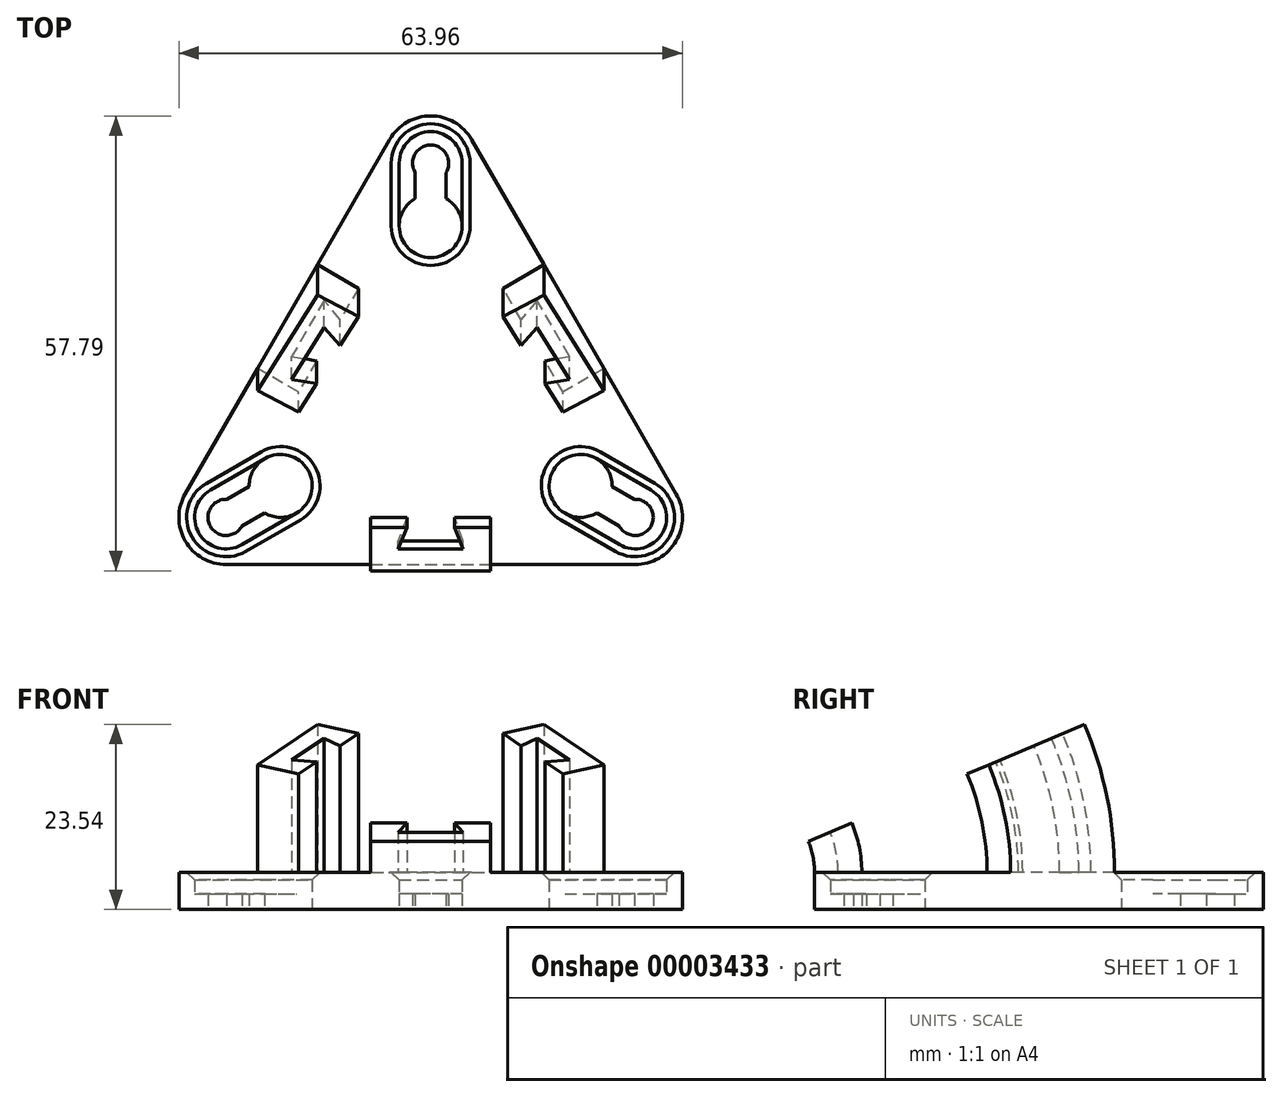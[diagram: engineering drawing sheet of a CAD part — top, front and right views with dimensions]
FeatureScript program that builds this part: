
annotation { "Feature Type Name" : "Feature", "Feature Type Description" : "" }
export const myFeature = defineFeature(function(context is Context, id is Id, definition is map)
    precondition{}
    {
        {
            var Q0;
            Q0=qCreatedBy(makeId("Top.planeOp"),FACE);
            cPlane(context, id + "F0", {"entities" : qUnion([Q0]), "cplaneType" : CPlaneType.OFFSET, "offset" : 2 * mm, "width" : 150 * mm, "height" : 150 * mm});
        }
        {
            var Q0;
            Q0=qCreatedBy(id+"F0.planeOp",FACE);
            cPlane(context, id + "F1", {"entities" : qUnion([Q0]), "cplaneType" : CPlaneType.OFFSET, "offset" : 2.75 * mm, "width" : 150 * mm, "height" : 150 * mm});
        }
        {
            var Q0;
            Q0=qCreatedBy(makeId("Top.planeOp"),FACE);
            var sketch = newSketch(context, id + "F2", { "sketchPlane" : qUnion([Q0])});
            skCircle(sketch, "E0.cCircle", {"center": v(0, 0) * mm, "radius": 30 * mm, "construction": true});
            skLineSegment(sketch, "E0.0", {"start": v(0, 30) * mm, "end": v(25.98, -15) * mm, "construction": true});
            skLineSegment(sketch, "E0.1", {"start": v(25.98, -15) * mm, "end": v(-25.98, -15) * mm, "construction": true});
            skLineSegment(sketch, "E0.2", {"start": v(-25.98, -15) * mm, "end": v(0, 30) * mm, "construction": true});
            skArc(sketch, "E1", {"start": v(1.95, 28.78) * mm, "mid": v(2.3, 29.96) * mm, "end": v(2, 31.15) * mm});
            skArc(sketch, "E2", {"start": v(-1.95, 25.5) * mm, "mid": v(0, 18) * mm, "end": v(1.95, 25.5) * mm});
            skLineSegment(sketch, "E3", {"start": v(-1.95, 28.78) * mm, "end": v(-1.95, 25.5) * mm});
            skLineSegment(sketch, "E4", {"start": v(0, 30) * mm, "end": v(0, 22) * mm, "construction": true});
            skLineSegment(sketch, "E5.0.MirrorCS", {"start": v(1.95, 28.78) * mm, "end": v(1.95, 25.5) * mm});
            skLineSegment(sketch, "E6.1.0", {"start": v(-25.98, -15) * mm, "end": v(-19.05, -11) * mm, "construction": true});
            skArc(sketch, "E6.1.1", {"start": v(-21.1, -14.43) * mm, "mid": v(-15.59, -9) * mm, "end": v(-23.05, -11.06) * mm});
            skLineSegment(sketch, "E6.1.2", {"start": v(-23.95, -16.08) * mm, "end": v(-21.1, -14.43) * mm});
            skArc(sketch, "E6.1.3", {"start": v(-25.9, -12.7) * mm, "mid": v(-27.1, -12.99) * mm, "end": v(-27.97, -13.85) * mm});
            skLineSegment(sketch, "E6.1.4", {"start": v(-25.9, -12.7) * mm, "end": v(-23.05, -11.06) * mm});
            skLineSegment(sketch, "E6.2.0", {"start": v(25.98, -15) * mm, "end": v(19.05, -11) * mm, "construction": true});
            skArc(sketch, "E6.2.1", {"start": v(23.05, -11.06) * mm, "mid": v(15.59, -9) * mm, "end": v(21.1, -14.43) * mm});
            skLineSegment(sketch, "E6.2.2", {"start": v(25.9, -12.7) * mm, "end": v(23.05, -11.06) * mm});
            skArc(sketch, "E6.2.3", {"start": v(23.95, -16.08) * mm, "mid": v(24.8, -16.97) * mm, "end": v(25.98, -17.3) * mm});
            skLineSegment(sketch, "E6.2.4", {"start": v(23.95, -16.08) * mm, "end": v(21.1, -14.43) * mm});
            skArc(sketch, "E7", {"start": v(-2, 31.15) * mm, "mid": v(-2.3, 29.96) * mm, "end": v(-1.95, 28.78) * mm});
            skArc(sketch, "E8", {"start": v(2, 31.15) * mm, "mid": v(0, 32.3) * mm, "end": v(-2, 31.15) * mm});
            skArc(sketch, "E9", {"start": v(27.97, -13.85) * mm, "mid": v(27.1, -12.99) * mm, "end": v(25.9, -12.7) * mm});
            skArc(sketch, "E10", {"start": v(25.98, -17.3) * mm, "mid": v(27.97, -16.15) * mm, "end": v(27.97, -13.85) * mm});
            skArc(sketch, "E11", {"start": v(-25.98, -17.3) * mm, "mid": v(-24.8, -16.97) * mm, "end": v(-23.95, -16.08) * mm});
            skArc(sketch, "E12", {"start": v(-27.97, -13.85) * mm, "mid": v(-27.97, -16.15) * mm, "end": v(-25.98, -17.3) * mm});
            skLineSegment(sketch, "E13", {"start": v(-29.44, -13) * mm, "end": v(-3.46, 32) * mm, "construction": true});
            skLineSegment(sketch, "E14", {"start": v(3.46, 32) * mm, "end": v(29.44, -13) * mm, "construction": true});
            skLineSegment(sketch, "E15", {"start": v(-25.98, -19) * mm, "end": v(25.98, -19) * mm, "construction": true});
            skArc(sketch, "E16", {"start": v(-3.46, 32) * mm, "mid": v(0, 26) * mm, "end": v(3.46, 32) * mm, "construction": true});
            skArc(sketch, "E17", {"start": v(3.46, 32) * mm, "mid": v(0, 34) * mm, "end": v(-3.46, 32) * mm, "construction": true});
            skArc(sketch, "E18", {"start": v(29.44, -13) * mm, "mid": v(22.52, -13) * mm, "end": v(25.98, -19) * mm, "construction": true});
            skArc(sketch, "E19", {"start": v(25.98, -19) * mm, "mid": v(29.44, -17) * mm, "end": v(29.44, -13) * mm, "construction": true});
            skArc(sketch, "E20", {"start": v(-25.98, -19) * mm, "mid": v(-22.52, -13) * mm, "end": v(-29.44, -13) * mm, "construction": true});
            skArc(sketch, "E21", {"start": v(-29.44, -13) * mm, "mid": v(-29.44, -17) * mm, "end": v(-25.98, -19) * mm, "construction": true});
            skLineSegment(sketch, "E22.0", {"start": v(-31.18, -12) * mm, "end": v(-5.2, 33) * mm});
            skArc(sketch, "E22.1", {"start": v(-31.18, -12) * mm, "mid": v(-31.18, -18) * mm, "end": v(-25.98, -21) * mm});
            skLineSegment(sketch, "E22.2", {"start": v(-25.98, -21) * mm, "end": v(25.98, -21) * mm});
            skArc(sketch, "E22.3", {"start": v(25.98, -21) * mm, "mid": v(31.18, -18) * mm, "end": v(31.18, -12) * mm});
            skLineSegment(sketch, "E22.4", {"start": v(5.2, 33) * mm, "end": v(31.18, -12) * mm});
            skArc(sketch, "E22.5", {"start": v(5.2, 33) * mm, "mid": v(0, 36) * mm, "end": v(-5.2, 33) * mm});
            skCircle(sketch, "E23", {"center": v(25.98, -15) * mm, "radius": 12 * mm, "construction": true});
            skCircle(sketch, "E24", {"center": v(-25.98, -15) * mm, "radius": 12 * mm, "construction": true});
            skCircle(sketch, "E25", {"center": v(0, 30) * mm, "radius": 12 * mm, "construction": true});
            skLineSegment(sketch, "E26", {"start": v(-25.98, -27) * mm, "end": v(25.98, -27) * mm, "construction": true});
            skSolve(sketch);
        }
        {
            var Q0;
            Q0=makeQuery(id+"F2.imprint","IMPRINT",FACE,{"disambiguationData":[TD([[makeQuery(id+"F2.imprint","IMPRINT",EDGE,{"derivedFrom":sQuery(id+"F2.wireOp",EDGE,"E1")}),-1.0]])]});
            var Q1;
            Q1=qCreatedBy(id+"F0.planeOp",FACE);
            extrude(context, id + "F3", {"entities" : qUnion([Q0]), "endBound" : BoundingType.UP_TO_SURFACE, "endBoundEntityFace" : qUnion([Q1]), "depth" : 25 * mm});
        }
        {
            var Q0;
            Q0=qCreatedBy(id+"F0.planeOp",FACE);
            var sketch = newSketch(context, id + "F4", { "sketchPlane" : qUnion([Q0])});
            skArc(sketch, "E27.0", {"start": v(-1.95, 25.5) * mm, "mid": v(-3.45, 24.02) * mm, "end": v(-4, 22) * mm, "construction": true});
            skLineSegment(sketch, "E27.1", {"start": v(-1.95, 28.78) * mm, "end": v(-1.95, 25.5) * mm, "construction": true});
            skArc(sketch, "E27.2", {"start": v(-2, 31.15) * mm, "mid": v(-2.3, 29.96) * mm, "end": v(-1.95, 28.78) * mm, "construction": true});
            skArc(sketch, "E27.3", {"start": v(2, 31.15) * mm, "mid": v(0, 32.3) * mm, "end": v(-2, 31.15) * mm, "construction": true});
            skArc(sketch, "E27.4", {"start": v(1.95, 28.78) * mm, "mid": v(2.3, 29.96) * mm, "end": v(2, 31.15) * mm, "construction": true});
            skArc(sketch, "E27.5", {"start": v(-3.46, 32) * mm, "mid": v(-3.86, 31.04) * mm, "end": v(-4, 30) * mm});
            skArc(sketch, "E27.6", {"start": v(3.46, 32) * mm, "mid": v(0, 34) * mm, "end": v(-3.46, 32) * mm});
            skLineSegment(sketch, "E27.7", {"start": v(1.95, 28.78) * mm, "end": v(1.95, 25.5) * mm, "construction": true});
            skLineSegment(sketch, "E28", {"start": v(-4, 30) * mm, "end": v(-4, 22) * mm});
            skLineSegment(sketch, "E29", {"start": v(4, 22) * mm, "end": v(4, 30) * mm});
            skArc(sketch, "E30.trimOffspring", {"start": v(4, 30) * mm, "mid": v(3.86, 31.04) * mm, "end": v(3.46, 32) * mm});
            skArc(sketch, "E31", {"start": v(-4, 22) * mm, "mid": v(0, 18) * mm, "end": v(4, 22) * mm});
            skArc(sketch, "E32", {"start": v(4, 22) * mm, "mid": v(3.45, 24.02) * mm, "end": v(1.95, 25.5) * mm, "construction": true});
            skArc(sketch, "E33.0", {"start": v(5.2, 33) * mm, "mid": v(0, 36) * mm, "end": v(-5.2, 33) * mm});
            skLineSegment(sketch, "E33.1", {"start": v(-31.18, -12) * mm, "end": v(-5.2, 33) * mm});
            skArc(sketch, "E33.2", {"start": v(-31.18, -12) * mm, "mid": v(-31.18, -18) * mm, "end": v(-25.98, -21) * mm});
            skLineSegment(sketch, "E33.3", {"start": v(-25.98, -21) * mm, "end": v(25.98, -21) * mm});
            skArc(sketch, "E33.4", {"start": v(25.98, -21) * mm, "mid": v(31.18, -18) * mm, "end": v(31.18, -12) * mm});
            skLineSegment(sketch, "E33.5", {"start": v(5.2, 33) * mm, "end": v(31.18, -12) * mm});
            skLineSegment(sketch, "E34.1.0", {"start": v(-23.98, -18.46) * mm, "end": v(-17.05, -14.46) * mm});
            skArc(sketch, "E34.1.1", {"start": v(-25.98, -19) * mm, "mid": v(-24.95, -18.86) * mm, "end": v(-23.98, -18.46) * mm});
            skArc(sketch, "E34.1.2", {"start": v(-29.44, -13) * mm, "mid": v(-29.44, -17) * mm, "end": v(-25.98, -19) * mm});
            skArc(sketch, "E34.1.3", {"start": v(-27.98, -11.54) * mm, "mid": v(-28.8, -12.17) * mm, "end": v(-29.44, -13) * mm});
            skLineSegment(sketch, "E34.1.4", {"start": v(-21.05, -7.54) * mm, "end": v(-27.98, -11.54) * mm});
            skArc(sketch, "E34.1.5", {"start": v(-17.05, -14.46) * mm, "mid": v(-15.59, -9) * mm, "end": v(-21.05, -7.54) * mm});
            skLineSegment(sketch, "E34.2.0", {"start": v(27.98, -11.54) * mm, "end": v(21.05, -7.54) * mm});
            skArc(sketch, "E34.2.1", {"start": v(29.44, -13) * mm, "mid": v(28.8, -12.17) * mm, "end": v(27.98, -11.54) * mm});
            skArc(sketch, "E34.2.2", {"start": v(25.98, -19) * mm, "mid": v(29.44, -17) * mm, "end": v(29.44, -13) * mm});
            skArc(sketch, "E34.2.3", {"start": v(23.98, -18.46) * mm, "mid": v(24.95, -18.86) * mm, "end": v(25.98, -19) * mm});
            skLineSegment(sketch, "E34.2.4", {"start": v(17.05, -14.46) * mm, "end": v(23.98, -18.46) * mm});
            skArc(sketch, "E34.2.5", {"start": v(21.05, -7.54) * mm, "mid": v(15.59, -9) * mm, "end": v(17.05, -14.46) * mm});
            skPoint(sketch, "E34.center", {"position": v(0, 0) * mm});
            skSolve(sketch);
        }
        {
            var Q0;
            Q0=makeQuery(id+"F4.imprint","IMPRINT",FACE,{"disambiguationData":[TD([[makeQuery(id+"F4.imprint","IMPRINT",EDGE,{"derivedFrom":sQuery(id+"F4.wireOp",EDGE,"E27.5")}),-1.0]])]});
            var Q1;
            Q1=qCreatedBy(id+"F1.planeOp",FACE);
            extrude(context, id + "F5", {"entities" : qUnion([Q0]), "operationType" : NewBodyOperationType.ADD, "endBound" : BoundingType.UP_TO_SURFACE, "endBoundEntityFace" : qUnion([Q1]), "depth" : 25 * mm});
        }
        {
            var Q0;
            Q0=qCreatedBy(id+"F1.planeOp",FACE);
            var sketch = newSketch(context, id + "F6", { "sketchPlane" : qUnion([Q0])});
            skLineSegment(sketch, "E35", {"start": v(-7.62, -21) * mm, "end": v(7.62, -21) * mm});
            skLineSegment(sketch, "E36", {"start": v(0, 0) * mm, "end": v(0, -11.67) * mm, "construction": true});
            skPoint(sketch, "E37", {"position": v(0, -21) * mm});
            skLineSegment(sketch, "E38", {"start": v(-7.62, -21) * mm, "end": v(-7.62, -15) * mm});
            skLineSegment(sketch, "E39", {"start": v(-7.62, -15) * mm, "end": v(-3.02, -15) * mm});
            skLineSegment(sketch, "E40", {"start": v(-3.02, -15) * mm, "end": v(-4.12, -18) * mm});
            skLineSegment(sketch, "E41", {"start": v(-4.12, -18) * mm, "end": v(4.12, -18) * mm});
            skLineSegment(sketch, "E42", {"start": v(4.12, -18) * mm, "end": v(3.02, -15) * mm});
            skLineSegment(sketch, "E43", {"start": v(3.02, -15) * mm, "end": v(7.62, -15) * mm});
            skLineSegment(sketch, "E44", {"start": v(7.62, -15) * mm, "end": v(7.62, -21) * mm});
            skPoint(sketch, "E45", {"position": v(-7.62, -18) * mm});
            skPoint(sketch, "E46", {"position": v(0, -18) * mm});
            skLineSegment(sketch, "E47.1.0", {"start": v(22, 3.9) * mm, "end": v(16.8, 0.9) * mm});
            skLineSegment(sketch, "E47.1.1", {"start": v(16.8, 0.9) * mm, "end": v(14.5, 4.88) * mm});
            skLineSegment(sketch, "E47.1.2", {"start": v(14.5, 4.88) * mm, "end": v(17.65, 5.43) * mm});
            skLineSegment(sketch, "E47.1.3", {"start": v(17.65, 5.43) * mm, "end": v(13.53, 12.57) * mm});
            skLineSegment(sketch, "E47.1.4", {"start": v(13.53, 12.57) * mm, "end": v(11.48, 10.12) * mm});
            skLineSegment(sketch, "E47.1.5", {"start": v(11.48, 10.12) * mm, "end": v(9.18, 14.1) * mm});
            skLineSegment(sketch, "E47.1.6", {"start": v(9.18, 14.1) * mm, "end": v(14.38, 17.1) * mm});
            skLineSegment(sketch, "E47.1.7", {"start": v(22, 3.9) * mm, "end": v(14.38, 17.1) * mm});
            skLineSegment(sketch, "E47.2.0", {"start": v(-14.38, 17.1) * mm, "end": v(-9.18, 14.1) * mm});
            skLineSegment(sketch, "E47.2.1", {"start": v(-9.18, 14.1) * mm, "end": v(-11.48, 10.12) * mm});
            skLineSegment(sketch, "E47.2.2", {"start": v(-11.48, 10.12) * mm, "end": v(-13.53, 12.57) * mm});
            skLineSegment(sketch, "E47.2.3", {"start": v(-13.53, 12.57) * mm, "end": v(-17.65, 5.43) * mm});
            skLineSegment(sketch, "E47.2.4", {"start": v(-17.65, 5.43) * mm, "end": v(-14.5, 4.88) * mm});
            skLineSegment(sketch, "E47.2.5", {"start": v(-14.5, 4.88) * mm, "end": v(-16.8, 0.9) * mm});
            skLineSegment(sketch, "E47.2.6", {"start": v(-16.8, 0.9) * mm, "end": v(-22, 3.9) * mm});
            skLineSegment(sketch, "E47.2.7", {"start": v(-14.38, 17.1) * mm, "end": v(-22, 3.9) * mm});
            skPoint(sketch, "E47.center", {"position": v(0, 0) * mm});
            skLineSegment(sketch, "E48", {"start": v(-7.62, -31) * mm, "end": v(7.62, -31) * mm, "construction": true});
            skSolve(sketch);
        }
        {
            var Q0;
            Q0=makeQuery(id+"F6.imprint","IMPRINT",FACE,{"disambiguationData":[TD([[makeQuery(id+"F6.imprint","IMPRINT",EDGE,{"derivedFrom":sQuery(id+"F6.wireOp",EDGE,"E47.2.0")}),-1.0]])]});
            var Q1;
            Q1=makeQuery(id+"F6.imprint","IMPRINT",FACE,{"disambiguationData":[TD([[makeQuery(id+"F6.imprint","IMPRINT",EDGE,{"derivedFrom":sQuery(id+"F6.wireOp",EDGE,"E35")}),1.0]])]});
            var Q2;
            Q2=makeQuery(id+"F6.imprint","IMPRINT",FACE,{"disambiguationData":[TD([[makeQuery(id+"F6.imprint","IMPRINT",EDGE,{"derivedFrom":sQuery(id+"F6.wireOp",EDGE,"E47.1.0")}),-1.0]])]});
            var Q3;
            Q3=sQuery(id+"F6.wireOp",EDGE,"E48");
            revolve(context, id + "F7", {"operationType" : NewBodyOperationType.ADD, "entities" : qUnion([Q0, Q1, Q2]), "axis" : qUnion([Q3]), "revolveType" : RevolveType.ONE_DIRECTION, "angle" : 23 * degree});
        }
        {
            var Q0;
            Q0=makeQuery(id+"F5.opExtrude","CAP_EDGE",EDGE,{"disambiguationData":[OSD([sQuery(id+"F4.wireOp",EDGE,"E34.1.1"),sQuery(id+"F4.wireOp",EDGE,"E34.1.2"),sQuery(id+"F4.wireOp",EDGE,"E34.1.3")])],"isStart":false});
            var Q1;
            Q1=makeQuery(id+"F5.opExtrude","CAP_EDGE",EDGE,{"disambiguationData":[OSD([sQuery(id+"F4.wireOp",EDGE,"E31")])],"isStart":false});
            var Q2;
            Q2=makeQuery(id+"F5.opExtrude","CAP_EDGE",EDGE,{"disambiguationData":[OSD([sQuery(id+"F4.wireOp",EDGE,"E34.2.5")])],"isStart":false});
            var Q3;
            Q3=makeQuery(id+"F7.opRevolve","CAP_EDGE",EDGE,{"disambiguationData":[OSD([sQuery(id+"F6.wireOp",EDGE,"E47.1.0")])],"isStart":true});
            var Q4;
            Q4=makeQuery(id+"F7.opRevolve","CAP_EDGE",EDGE,{"disambiguationData":[OSD([sQuery(id+"F6.wireOp",EDGE,"E44")])],"isStart":true});
            var Q5;
            Q5=makeQuery(id+"F7.opRevolve","CAP_EDGE",EDGE,{"disambiguationData":[OSD([sQuery(id+"F6.wireOp",EDGE,"E38")])],"isStart":true});
            var Q6;
            Q6=makeQuery(id+"F7.opRevolve","CAP_EDGE",EDGE,{"disambiguationData":[OSD([sQuery(id+"F6.wireOp",EDGE,"E47.2.6")])],"isStart":true});
            var Q7;
            Q7=makeQuery(id+"F7.opRevolve","CAP_EDGE",EDGE,{"disambiguationData":[OSD([sQuery(id+"F6.wireOp",EDGE,"E47.1.6")])],"isStart":true});
            var Q8;
            Q8=makeQuery(id+"F7.opRevolve","CAP_EDGE",EDGE,{"disambiguationData":[OSD([sQuery(id+"F6.wireOp",EDGE,"E47.2.0")])],"isStart":true});
            chamfer(context, id + "F8", {"entities" : qUnion([Q0, Q1, Q2, Q3, Q4, Q5, Q6, Q7, Q8]), "width" : 1 * mm, "tangentPropagation" : true});
        }
    });
